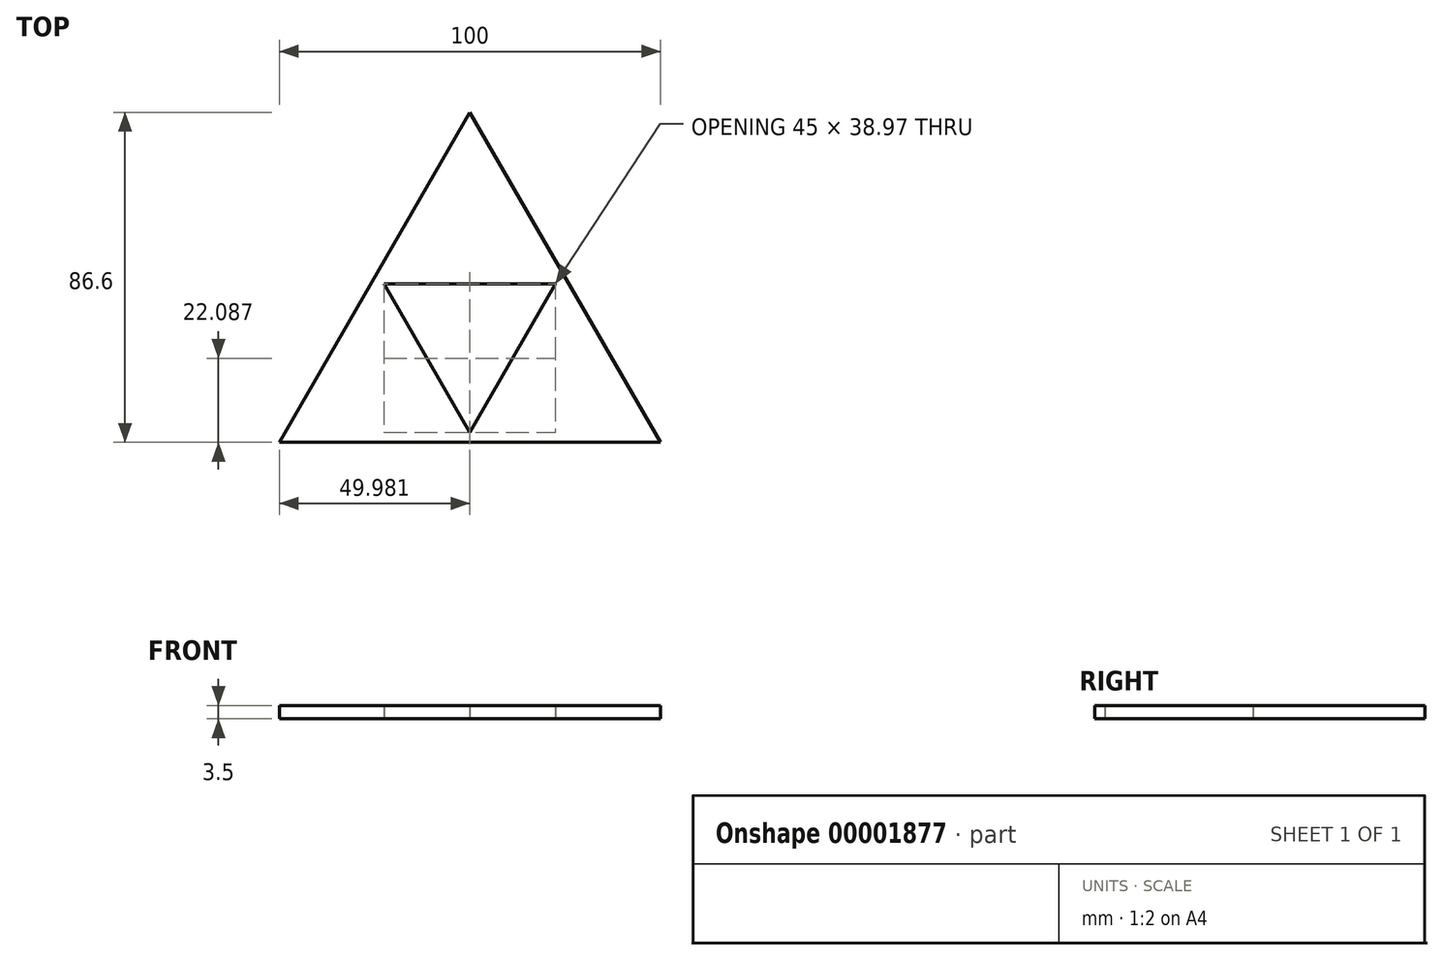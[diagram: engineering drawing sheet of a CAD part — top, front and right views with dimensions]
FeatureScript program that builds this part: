
annotation { "Feature Type Name" : "Feature", "Feature Type Description" : "" }
export const myFeature = defineFeature(function(context is Context, id is Id, definition is map)
    precondition{}
    {
        {
            var Q0;
            Q0=qCreatedBy(makeId("Top.planeOp"),FACE);
            var sketch = newSketch(context, id + "F0", { "sketchPlane" : qUnion([Q0])});
            skLineSegment(sketch, "E0", {"start": v(0, 54.74) * mm, "end": v(-50, -31.86) * mm});
            skLineSegment(sketch, "E1", {"start": v(-50, -31.86) * mm, "end": v(50, -31.86) * mm});
            skLineSegment(sketch, "E2", {"start": v(50, -31.86) * mm, "end": v(0, 54.74) * mm});
            skLineSegment(sketch, "E3", {"start": v(-0.02, -29.26) * mm, "end": v(-22.52, 9.71) * mm});
            skLineSegment(sketch, "E4", {"start": v(-22.52, 9.71) * mm, "end": v(22.48, 9.71) * mm});
            skLineSegment(sketch, "E5", {"start": v(22.48, 9.71) * mm, "end": v(-0.02, -29.26) * mm});
            skSolve(sketch);
        }
        {
            var Q0;
            Q0=makeQuery(id+"F0.imprint","IMPRINT",FACE,{"disambiguationData":[TD([[makeQuery(id+"F0.imprint","IMPRINT",EDGE,{"derivedFrom":sQuery(id+"F0.wireOp",EDGE,"E0")}),1.0]])]});
            extrude(context, id + "F1", {"entities" : qUnion([Q0]), "depth" : 3.5 * mm, "offsetDistance" : 25 * mm});
        }
    });
